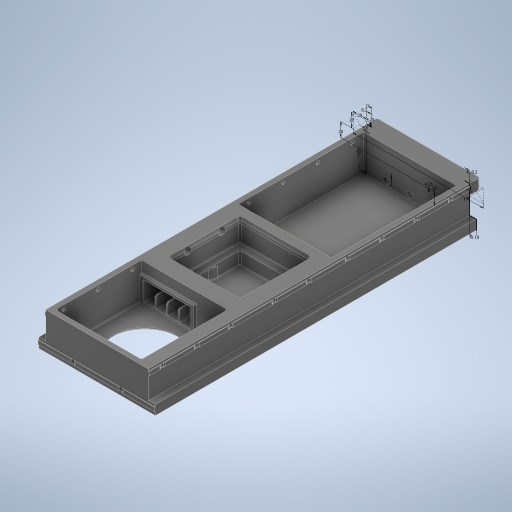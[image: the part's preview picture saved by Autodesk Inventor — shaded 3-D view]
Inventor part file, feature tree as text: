
AUTODESK INVENTOR PART (.ipt)
format: ipt  version: 2024 (Build 280153000, 153)  size: 1,603,584 bytes
history: native  units: mm
features: projected_geometry x33, sketch x27, extrude x26, fillet x17, hole x8, chamfer x6, plane x3, thicken_offset x3, other x3, mirror x2
ambient origin geometry x8: Origin, YZ Plane, XZ Plane, XY Plane, X Axis, Y Axis, Z Axis, Center Point
bodies: Solid1 (feature_tree)
feature tree (128):
  sketch  "Sketch1"  dims[d0=20.0mm d1=20.0mm]
  extrude  "Extrusion1"  Depth=20.0mm
  extrude  "Extrusion2"  Depth=20.0mm
  extrude  "Extrusion3"  Depth=18.0mm
  extrude  "Extrusion31"  Depth=10.0mm
  fillet  "Fillet5"  Radius=0.2mm
  fillet  "Fillet39"  Radius=0.2mm
  hole  "Hole3"  [1 undecoded]
  extrude  "Extrusion7"  Depth=2.0mm
  extrude  "Extrusion8"  Depth=1.0mm
  extrude  "Extrusion9"  Depth=1.0mm
  extrude  "Extrusion13"  Depth=1.0mm
  sketch  "Sketch17"  dims[d21=5.5mm d22=1.0mm]
  extrude  "Extrusion12"  Depth=2.0mm
  extrude  "Extrusion16"  Depth=2.0mm
  extrude  "Extrusion18"  Depth=5.5mm
  extrude  "Extrusion19"  Depth=6.0mm
  chamfer  "Chamfer2"  [1 undecoded]
  extrude  "Extrusion20"  Depth=105.0mm
  hole  "Hole6"  [1 undecoded]
  sketch  "Sketch25"  dims[d60=5.4mm d61=6.0mm d62=4.0mm d63=2.0mm d64=90.0deg d65=8.0mm d66=150.0deg d67=9.5mm]
  plane  "Work Plane2"
  extrude  "Extrusion21"  Depth=120.0mm
  sketch  "Sketch26"  dims[d68=5.0mm d69=0.0mm d70=5.5mm]
  plane  "Work Plane3"
  extrude  "Extrusion22"  TaperAngle=0.0deg  [1 undecoded]
  extrude  "Extrusion23"  Depth=2.8mm
  extrude  "Extrusion24"  Depth=2.8mm
  fillet  "Fillet13"  Radius=2.8mm
  sketch  "Sketch28"  dims[d92=90.0mm d93=105.0mm]
  thicken_offset  "Thicken1"
  thicken_offset  "Thicken2"
  thicken_offset  "Thicken3"
  extrude  "Extrusion25"  Depth=101.0mm
  extrude  "Extrusion26"  Depth=15.0mm
  extrude  "Extrusion27"  Depth=78.0mm
  fillet  "Fillet15"  Radius=0.5mm
  chamfer  "Chamfer4"  Distance=10.0mm
  fillet  "Fillet16"  Radius=27.5mm
  fillet  "Fillet17"  Radius=34.0mm
  extrude  "Extrusion28"  Depth=2.0mm
  fillet  "Fillet19"  Radius=25.0mm
  fillet  "Fillet23"  Radius=80.0mm
  fillet  "Fillet26"  Radius=80.0mm
  fillet  "Fillet27"  [1 undecoded]
  fillet  "Fillet28"  Radius=25.0mm
  fillet  "Fillet33"  Radius=20.0mm
  fillet  "Fillet34"  [1 undecoded]
  fillet  "Fillet35"  Radius=10.0mm
  fillet  "Fillet36"  [1 undecoded]
  fillet  "Fillet37"  Radius=5.0mm
  extrude  "Extrusion29"  Depth=15.0mm
  chamfer  "Chamfer5"  Distance=40.0mm
  chamfer  "Chamfer6"  [1 undecoded]
  sketch  "Sketch36"  dims[d126=101.0mm d127=101.0mm]
  hole  "Hole7"  [1 undecoded]
  hole  "Hole8"  [1 undecoded]
  mirror  "Mirror3"
  chamfer  "Chamfer7"  Distance=30.0mm
  extrude  "Extrusion30"  Depth=2.0mm
  hole  "Hole9"  [1 undecoded]
  fillet  "Fillet38"  Radius=4.0mm
  hole  "Hole10"  [1 undecoded]
  chamfer  "Chamfer8"  Distance=34.0mm
  hole  "Hole11"  [1 undecoded]
  mirror  "Mirror4"
  plane  "Work Plane5"
  hole  "Hole12"  [1 undecoded]
  sketch  "Sketch2"  dims[d4=190.0mm d5=20.0mm]
  projected_geometry  "Projected Loop1"
  sketch  "Sketch3"  dims[d6=4.25mm d7=18.0mm]
  projected_geometry  "Projected Loop2"
  sketch  "Sketch10"  dims[d8=10.0mm d9=10.0mm d10=0.2mm d11=0.2mm]
  sketch  "Sketch11"  dims[d12=4.25mm d13=7.0mm]
  projected_geometry  "Projected Loop7"
  sketch  "Sketch12"  dims[d14=10.0mm d16=2.0mm]
  projected_geometry  "Projected Loop8"
  sketch  "Sketch13"  dims[d18=468.2mm d19=0.0mm d20=1.0mm]
  projected_geometry  "Projected Loop9"
  sketch  "Sketch18"  dims[d23=7.0mm d24=0.0mm d25=1.0mm]
  projected_geometry  "Projected Loop13"
  sketch  "Sketch23"  dims[d26=15.0mm d27=0.0mm d39=2.0mm]
  projected_geometry  "Projected Loop19"
  sketch  "Sketch24"  dims[d59=70.0mm]
  projected_geometry  "Projected Loop20"
  projected_geometry  "Projected Loop21"
  projected_geometry  "Projected Loop22"
  projected_geometry  "Projected Loop23"
  projected_geometry  "Projected Loop24"
  projected_geometry  "Projected Loop25"
  projected_geometry  "Projected Loop26"
  sketch  "Sketch27"  dims[d71=1.0mm d72=0.0mm d73=6.0mm d74=0.0mm d75=0.0mm]
  projected_geometry  "Projected Loop27"
  projected_geometry  "Projected Loop28"
  other  "Srf1"
  other  "Srf2"
  other  "Srf3"
  sketch  "Sketch29"  dims[d94=105.0mm d95=47.5mm]
  projected_geometry  "Projected Loop29"
  sketch  "Sketch30"  dims[d96=120.0mm d97=120.0mm]
  projected_geometry  "Projected Loop30"
  sketch  "Sketch31"  dims[d99=52.5mm d100=0.0mm d101=0.0mm]
  projected_geometry  "Projected Loop31"
  sketch  "Sketch32"  dims[d102=7.0mm d103=0.0mm d122=2.8mm]
  projected_geometry  "Projected Loop32"
  sketch  "Sketch33"  dims[d123=2.8mm d124=2.8mm d125=2.8mm]
  projected_geometry  "Projected Loop33"
  projected_geometry  "Projected Loop34"
  projected_geometry  "Projected Loop35"
  projected_geometry  "Projected Loop36"
  projected_geometry  "Projected Loop37"
  sketch  "Sketch38"  dims[d128=15.0mm d129=25.0mm]
  sketch  "Sketch39"  dims[d130=9.0mm d131=78.0mm d132=0.5mm]
  sketch  "Sketch40"  dims[d133=150.0mm d134=10.0mm d135=0.0mm d143=27.5mm d144=0.0mm d145=34.0mm d146=0.0mm]
  sketch  "Sketch41"  dims[d147=2.3mm d148=2.0mm d149=45.0deg d150=14.0mm d156=25.0mm d157=0.0mm]
  projected_geometry  "Projected Loop38"
  projected_geometry  "Projected Loop39"
  sketch  "Sketch42"  dims[d163=4.4mm d164=6.0mm d165=4.0mm d166=2.0mm d167=90.0deg d168=8.0mm d169=150.0deg d170=80.0mm d171=80.0mm d172=-32.0mm d173=25.0mm d174=0.0mm d175=20.0mm d176=150.0deg d177=10.0mm d178=135.0deg d179=5.0mm]
  projected_geometry  "Projected Loop40"
  projected_geometry  "Projected Loop41"
  projected_geometry  "Projected Loop42"
  sketch  "Sketch43"  dims[d180=5.0mm d182=15.0mm d183=40.0mm d184=-2.0mm d185=10.0mm d186=0.0mm d187=2.0mm d188=30.0mm d189=0.0mm d191=12.0mm d194=30.0mm d195=0.0mm d196=4.0mm d197=45.0deg d198=34.0mm d199=17.0mm d200=17.0mm d201=15.0deg d202=0.654498mm d203=0.654498mm d205=0.654498mm d206=15.0mm d207=19.0mm d208=0.0mm d209=19.0mm d210=0.0mm d211=19.0mm d212=0.0mm d213=2.0mm d214=2.0mm d215=2.0mm d216=2.0mm d217=10.0mm d218=0.0mm d219=10.0mm d220=0.0mm d221=10.0mm d222=0.0mm d223=2.0mm d224=6.0mm d225=2.0mm d226=3.490659mm d227=10.0mm d228=2.0mm d229=2.0mm d230=0.0mm d232=4.0mm d239=4.0mm d246=1.0mm d247=1.0mm d248=0.5mm d249=1.0mm d250=1.0mm d255=1.0mm d256=3.0mm d257=2.0mm d258=1.0mm d259=1.0mm d260=125.0mm d261=10.0mm d262=13.482833mm d263=13.482833mm d264=3.0mm d265=0.0mm d266=3.0mm d267=2.0mm d268=3.490659mm d281=4.0mm d282=2.0mm d283=3.490659mm d284=100.0mm d285=50.0mm d286=150.0mm d287=50.0mm d288=5.4mm d289=6.0mm d290=4.0mm d291=2.0mm d292=90.0deg d293=8.0mm d294=150.0deg d295=6.0mm d296=6.0mm d297=4.0mm d298=2.0mm d299=90.0deg d300=8.0mm d301=0.0mm d302=1.0mm d303=2.0mm d304=3.490659mm d305=5.4mm d306=6.0mm d307=4.0mm d308=2.0mm d309=90.0deg d310=20.0mm d311=150.0deg d312=1.0mm d313=1.0mm d314=0.0mm d315=6.0mm d316=6.0mm d317=4.0mm d318=2.0mm d319=90.0deg d320=20.0mm d321=0.0mm d322=1.0mm d323=2.0mm d324=3.490659mm d325=9.5mm d326=6.0mm d327=4.0mm d328=2.0mm d329=90.0deg d330=8.0mm d331=0.0mm d332=-7.0mm d333=9.5mm d334=6.0mm d335=4.0mm d336=2.0mm d337=90.0deg d338=8.0mm d339=0.0mm d340=15.0mm d341=0.0mm d342=2.0mm d139=0.0mm d140=0.0mm d141=0.0mm d142=0.0mm d251=0.0mm d252=0.0mm d253=0.0mm d254=0.0mm]
  projected_geometry  "Projected Loop43"
  extrude  "ExtrusionSrf1"  TaperAngle=15.0deg  [1 undecoded]
  extrude  "ExtrusionSrf2"  Depth=2.0mm
  extrude  "ExtrusionSrf3"  Depth=2.0mm
  projected_geometry  "Project Cut Edges2"
  projected_geometry  "Project Cut Edges3"
note: 15 required parameter values undecoded (feature->parameter linkage not recoverable at this tier; creation-order binding heuristic only, values carry confidence <= 0.55)
